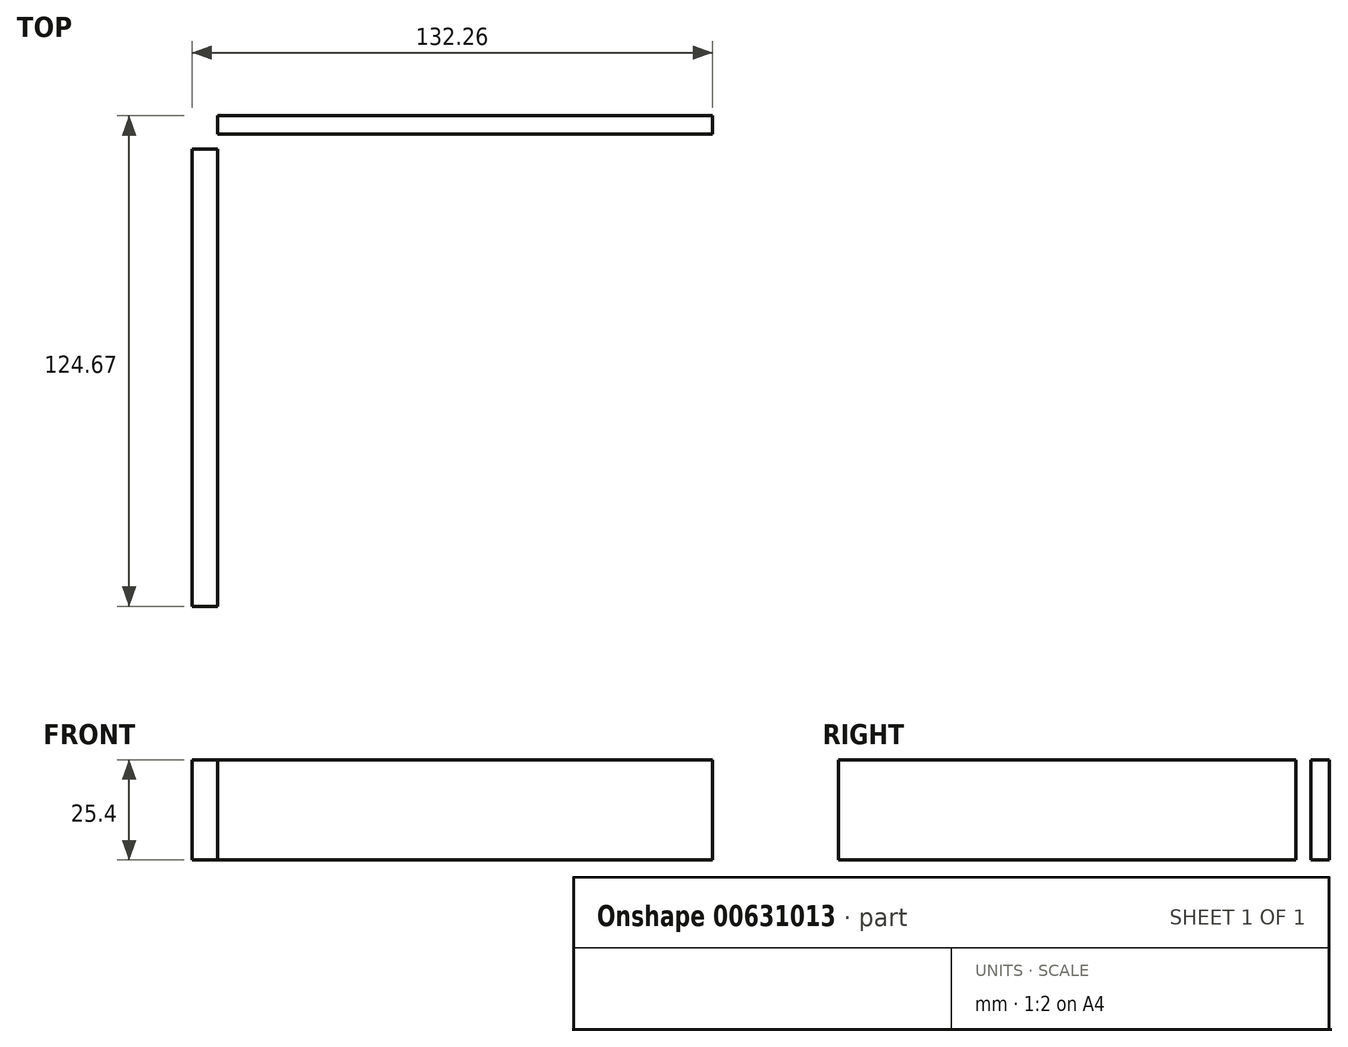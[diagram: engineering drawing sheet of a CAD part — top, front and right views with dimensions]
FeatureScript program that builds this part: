
annotation { "Feature Type Name" : "Feature", "Feature Type Description" : "" }
export const myFeature = defineFeature(function(context is Context, id is Id, definition is map)
    precondition{}
    {
        {
            var Q0;
            Q0=qCreatedBy(makeId("Top.planeOp"),FACE);
            var sketch = newSketch(context, id + "F0", { "sketchPlane" : qUnion([Q0])});
            skLineSegment(sketch, "E0.bottom", {"start": v(-67, 54.3) * mm, "end": v(-60.58, 54.3) * mm});
            skLineSegment(sketch, "E0.top", {"start": v(-67, -61.9) * mm, "end": v(-60.58, -61.9) * mm});
            skLineSegment(sketch, "E0.left", {"start": v(-67, 54.3) * mm, "end": v(-67, -61.9) * mm});
            skLineSegment(sketch, "E0.right", {"start": v(-60.58, 54.3) * mm, "end": v(-60.58, -61.9) * mm});
            skLineSegment(sketch, "E1.bottom", {"start": v(-60.58, 62.77) * mm, "end": v(65.25, 62.77) * mm});
            skLineSegment(sketch, "E1.top", {"start": v(-60.58, 58.1) * mm, "end": v(65.25, 58.1) * mm});
            skLineSegment(sketch, "E1.left", {"start": v(-60.58, 62.77) * mm, "end": v(-60.58, 58.1) * mm});
            skLineSegment(sketch, "E1.right", {"start": v(65.25, 62.77) * mm, "end": v(65.25, 58.1) * mm});
            skSolve(sketch);
        }
        {
            var Q0;
            Q0 = qSketchRegion(id + "F0", true);
            extrude(context, id + "F1", {"entities" : qUnion([Q0]), "depth" : 25.4 * mm, "offsetDistance" : 25.4 * mm});
        }
    });
